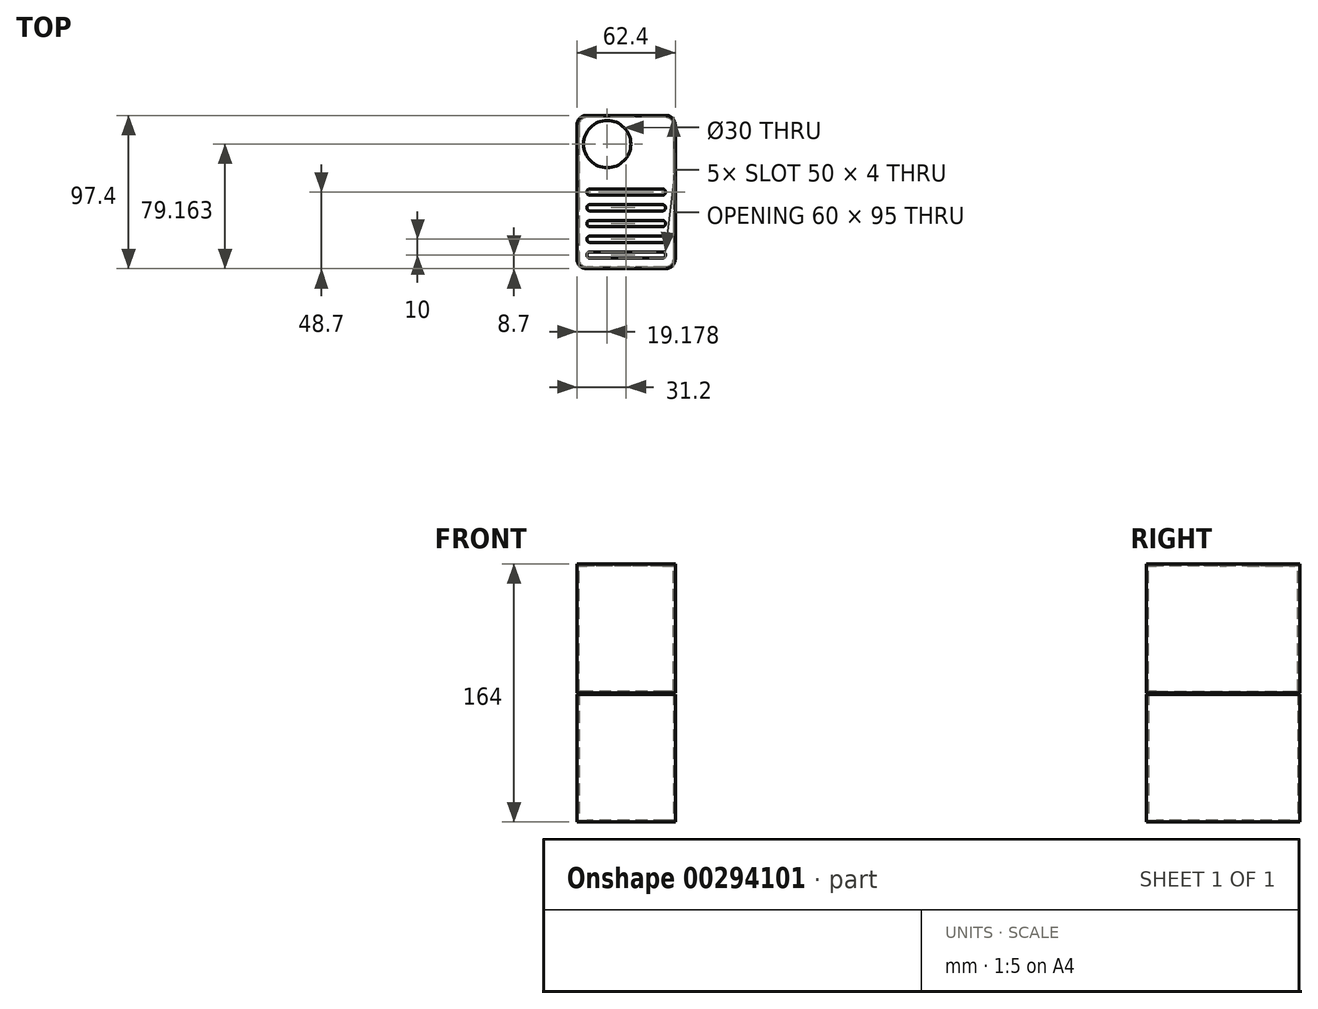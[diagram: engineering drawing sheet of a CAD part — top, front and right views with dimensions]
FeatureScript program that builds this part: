
annotation { "Feature Type Name" : "Feature", "Feature Type Description" : "" }
export const myFeature = defineFeature(function(context is Context, id is Id, definition is map)
    precondition{}
    {
        {
            var Q0;
            Q0=qCreatedBy(makeId("Top.planeOp"),FACE);
            var sketch = newSketch(context, id + "F0", { "sketchPlane" : qUnion([Q0])});
            skLineSegment(sketch, "E0.bottom", {"start": v(25, 47.5) * mm, "end": v(-25, 47.5) * mm});
            skLineSegment(sketch, "E0.top", {"start": v(25, -47.5) * mm, "end": v(-25, -47.5) * mm});
            skLineSegment(sketch, "E0.left", {"start": v(30, 42.5) * mm, "end": v(30, -42.5) * mm});
            skLineSegment(sketch, "E0.right", {"start": v(-30, 42.5) * mm, "end": v(-30, -42.5) * mm});
            skPoint(sketch, "E0.middle", {"position": v(0, 0) * mm});
            skPoint(sketch, "E1.visualSharp", {"position": v(-30, 47.5) * mm});
            skArc(sketch, "E1.filletArc", {"start": v(-25, 47.5) * mm, "mid": v(-28.54, 46.04) * mm, "end": v(-30, 42.5) * mm});
            skPoint(sketch, "E2.visualSharp", {"position": v(30, 47.5) * mm});
            skArc(sketch, "E2.filletArc", {"start": v(30, 42.5) * mm, "mid": v(28.54, 46.04) * mm, "end": v(25, 47.5) * mm});
            skPoint(sketch, "E3.visualSharp", {"position": v(30, -47.5) * mm});
            skArc(sketch, "E3.filletArc", {"start": v(25, -47.5) * mm, "mid": v(28.54, -46.04) * mm, "end": v(30, -42.5) * mm});
            skPoint(sketch, "E4.visualSharp", {"position": v(-30, -47.5) * mm});
            skArc(sketch, "E4.filletArc", {"start": v(-30, -42.5) * mm, "mid": v(-28.54, -46.04) * mm, "end": v(-25, -47.5) * mm});
            skArc(sketch, "E5.0", {"start": v(31.2, 42.5) * mm, "mid": v(29.38, 46.88) * mm, "end": v(25, 48.7) * mm});
            skLineSegment(sketch, "E5.1", {"start": v(31.2, 42.5) * mm, "end": v(31.2, -42.5) * mm});
            skLineSegment(sketch, "E5.2", {"start": v(25, 48.7) * mm, "end": v(-25, 48.7) * mm});
            skArc(sketch, "E5.3", {"start": v(25, -48.7) * mm, "mid": v(29.38, -46.88) * mm, "end": v(31.2, -42.5) * mm});
            skArc(sketch, "E5.4", {"start": v(-25, 48.7) * mm, "mid": v(-29.38, 46.88) * mm, "end": v(-31.2, 42.5) * mm});
            skLineSegment(sketch, "E5.5", {"start": v(-31.2, 42.5) * mm, "end": v(-31.2, -42.5) * mm});
            skArc(sketch, "E5.6", {"start": v(-31.2, -42.5) * mm, "mid": v(-29.38, -46.88) * mm, "end": v(-25, -48.7) * mm});
            skLineSegment(sketch, "E5.7", {"start": v(25, -48.7) * mm, "end": v(-25, -48.7) * mm});
            skSolve(sketch);
        }
        {
            var Q0;
            Q0 = qSketchRegion(id + "F0", true);
            extrude(context, id + "F1", {"entities" : qUnion([Q0]), "depth" : 82 * mm});
        }
        {
            var Q0;
            Q0=makeQuery(id+"F0.imprint","IMPRINT",FACE,{"disambiguationData":[TD([[makeQuery(id+"F0.imprint","IMPRINT",EDGE,{"derivedFrom":sQuery(id+"F0.wireOp",EDGE,"E0.bottom")}),1.0]])]});
            extrude(context, id + "F2", {"entities" : qUnion([Q0]), "operationType" : NewBodyOperationType.ADD, "depth" : 1.2 * mm});
        }
        {
            var Q0;
            Q0=makeQuery(id+"F1.opExtrude","CAP_FACE",FACE,{"disambiguationData":[OSD([sQuery(id+"F0.wireOp",EDGE,"E0.bottom"),sQuery(id+"F0.wireOp",EDGE,"E0.top"),sQuery(id+"F0.wireOp",EDGE,"E0.left"),sQuery(id+"F0.wireOp",EDGE,"E0.right"),sQuery(id+"F0.wireOp",EDGE,"E1.filletArc"),sQuery(id+"F0.wireOp",EDGE,"E2.filletArc"),sQuery(id+"F0.wireOp",EDGE,"E3.filletArc"),sQuery(id+"F0.wireOp",EDGE,"E4.filletArc"),sQuery(id+"F0.wireOp",EDGE,"E5.0"),sQuery(id+"F0.wireOp",EDGE,"E5.1"),sQuery(id+"F0.wireOp",EDGE,"E5.2"),sQuery(id+"F0.wireOp",EDGE,"E5.3"),sQuery(id+"F0.wireOp",EDGE,"E5.4"),sQuery(id+"F0.wireOp",EDGE,"E5.5"),sQuery(id+"F0.wireOp",EDGE,"E5.6"),sQuery(id+"F0.wireOp",EDGE,"E5.7")])],"isStart":false});
            var sketch = newSketch(context, id + "F3", { "sketchPlane" : qUnion([Q0])});
            skArc(sketch, "E6.0", {"start": v(-30.5, -42.5) * mm, "mid": v(-28.89, -46.39) * mm, "end": v(-25, -48) * mm});
            skLineSegment(sketch, "E6.1", {"start": v(-30.5, 42.5) * mm, "end": v(-30.5, -42.5) * mm});
            skLineSegment(sketch, "E6.2", {"start": v(-25, -48) * mm, "end": v(25, -48) * mm});
            skArc(sketch, "E6.3", {"start": v(-25, 48) * mm, "mid": v(-28.89, 46.39) * mm, "end": v(-30.5, 42.5) * mm});
            skArc(sketch, "E6.4", {"start": v(25, -48) * mm, "mid": v(28.89, -46.39) * mm, "end": v(30.5, -42.5) * mm});
            skLineSegment(sketch, "E6.5", {"start": v(30.5, -42.5) * mm, "end": v(30.5, 42.5) * mm});
            skArc(sketch, "E6.6", {"start": v(30.5, 42.5) * mm, "mid": v(28.89, 46.39) * mm, "end": v(25, 48) * mm});
            skLineSegment(sketch, "E6.7", {"start": v(25, 48) * mm, "end": v(-25, 48) * mm});
            skSolve(sketch);
        }
        {
            var Q0;
            Q0=makeQuery(id+"F3.imprint","IMPRINT",FACE,{"disambiguationData":[TD([[makeQuery(id+"F3.imprint","IMPRINT",EDGE,{"derivedFrom":sQuery(id+"F3.wireOp",EDGE,"E6.0")}),-1.0]])]});
            extrude(context, id + "F4", {"entities" : qUnion([Q0]), "operationType" : NewBodyOperationType.REMOVE, "oppositeDirection" : true, "depth" : 1 * mm});
        }
        {
            var Q0;
            Q0=makeQuery(id+"F1.opExtrude","SWEPT_BODY",BODY,{"disambiguationData":[OSD([sQuery(id+"F0.wireOp",EDGE,"E0.bottom"),sQuery(id+"F0.wireOp",EDGE,"E0.top"),sQuery(id+"F0.wireOp",EDGE,"E0.left"),sQuery(id+"F0.wireOp",EDGE,"E0.right"),sQuery(id+"F0.wireOp",EDGE,"E1.filletArc"),sQuery(id+"F0.wireOp",EDGE,"E2.filletArc"),sQuery(id+"F0.wireOp",EDGE,"E3.filletArc"),sQuery(id+"F0.wireOp",EDGE,"E4.filletArc"),sQuery(id+"F0.wireOp",EDGE,"E5.0"),sQuery(id+"F0.wireOp",EDGE,"E5.1"),sQuery(id+"F0.wireOp",EDGE,"E5.2"),sQuery(id+"F0.wireOp",EDGE,"E5.3"),sQuery(id+"F0.wireOp",EDGE,"E5.4"),sQuery(id+"F0.wireOp",EDGE,"E5.5"),sQuery(id+"F0.wireOp",EDGE,"E5.6"),sQuery(id+"F0.wireOp",EDGE,"E5.7")])]});
            var Q1;
            Q1=makeQuery(id+"F1.opExtrude","CAP_FACE",FACE,{"disambiguationData":[OSD([sQuery(id+"F0.wireOp",EDGE,"E0.bottom"),sQuery(id+"F0.wireOp",EDGE,"E0.top"),sQuery(id+"F0.wireOp",EDGE,"E0.left"),sQuery(id+"F0.wireOp",EDGE,"E0.right"),sQuery(id+"F0.wireOp",EDGE,"E1.filletArc"),sQuery(id+"F0.wireOp",EDGE,"E2.filletArc"),sQuery(id+"F0.wireOp",EDGE,"E3.filletArc"),sQuery(id+"F0.wireOp",EDGE,"E4.filletArc"),sQuery(id+"F0.wireOp",EDGE,"E5.0"),sQuery(id+"F0.wireOp",EDGE,"E5.1"),sQuery(id+"F0.wireOp",EDGE,"E5.2"),sQuery(id+"F0.wireOp",EDGE,"E5.3"),sQuery(id+"F0.wireOp",EDGE,"E5.4"),sQuery(id+"F0.wireOp",EDGE,"E5.5"),sQuery(id+"F0.wireOp",EDGE,"E5.6"),sQuery(id+"F0.wireOp",EDGE,"E5.7")])],"isStart":false});
            mirror(context, id + "F5", {"entities" : qUnion([Q0]), "mirrorPlane" : qUnion([Q1])});
        }
        {
            var Q0;
            Q0=makeQuery(id+"F5.opPattern","COPY",FACE,{"derivedFrom":makeQuery(id+"F4.boolean.opBoolean","COPY",FACE,{"derivedFrom":makeQuery(id+"F4.opExtrude","CAP_FACE",FACE,{"disambiguationData":[OSD([sQuery(id+"F0.wireOp",EDGE,"E5.0"),sQuery(id+"F0.wireOp",EDGE,"E5.1"),sQuery(id+"F0.wireOp",EDGE,"E5.2"),sQuery(id+"F0.wireOp",EDGE,"E5.3"),sQuery(id+"F0.wireOp",EDGE,"E5.4"),sQuery(id+"F0.wireOp",EDGE,"E5.5"),sQuery(id+"F0.wireOp",EDGE,"E5.6"),sQuery(id+"F0.wireOp",EDGE,"E5.7"),sQuery(id+"F3.wireOp",EDGE,"E6.0"),sQuery(id+"F3.wireOp",EDGE,"E6.1"),sQuery(id+"F3.wireOp",EDGE,"E6.2"),sQuery(id+"F3.wireOp",EDGE,"E6.3"),sQuery(id+"F3.wireOp",EDGE,"E6.4"),sQuery(id+"F3.wireOp",EDGE,"E6.5"),sQuery(id+"F3.wireOp",EDGE,"E6.6"),sQuery(id+"F3.wireOp",EDGE,"E6.7")])],"isStart":false})}),"instanceName":"1"});
            var sketch = newSketch(context, id + "F6", { "sketchPlane" : qUnion([Q0])});
            skArc(sketch, "E7.0", {"start": v(30.7, 42.5) * mm, "mid": v(29.03, 46.53) * mm, "end": v(25, 48.2) * mm});
            skLineSegment(sketch, "E7.1", {"start": v(30.7, -42.5) * mm, "end": v(30.7, 42.5) * mm});
            skLineSegment(sketch, "E7.2", {"start": v(25, 48.2) * mm, "end": v(-25, 48.2) * mm});
            skArc(sketch, "E7.3", {"start": v(25, -48.2) * mm, "mid": v(29.03, -46.53) * mm, "end": v(30.7, -42.5) * mm});
            skArc(sketch, "E7.4", {"start": v(-25, 48.2) * mm, "mid": v(-29.03, 46.53) * mm, "end": v(-30.7, 42.5) * mm});
            skLineSegment(sketch, "E7.5", {"start": v(-30.7, 42.5) * mm, "end": v(-30.7, -42.5) * mm});
            skArc(sketch, "E7.6", {"start": v(-30.7, -42.5) * mm, "mid": v(-29.03, -46.53) * mm, "end": v(-25, -48.2) * mm});
            skLineSegment(sketch, "E7.7", {"start": v(-25, -48.2) * mm, "end": v(25, -48.2) * mm});
            skSolve(sketch);
        }
        {
            var Q0;
            Q0=makeQuery(id+"F6.imprint","IMPRINT",FACE,{"disambiguationData":[TD([[makeQuery(id+"F6.imprint","IMPRINT",EDGE,{"derivedFrom":sQuery(id+"F6.wireOp",EDGE,"E7.0")}),-1.0]])]});
            extrude(context, id + "F7", {"entities" : qUnion([Q0]), "operationType" : NewBodyOperationType.ADD, "depth" : 1 * mm});
        }
        {
            var Q0;
            Q0=makeQuery(id+"F5.opPattern","COPY",FACE,{"derivedFrom":makeQuery(id+"F1.opExtrude","CAP_FACE",FACE,{"disambiguationData":[OSD([sQuery(id+"F0.wireOp",EDGE,"E0.bottom"),sQuery(id+"F0.wireOp",EDGE,"E0.top"),sQuery(id+"F0.wireOp",EDGE,"E0.left"),sQuery(id+"F0.wireOp",EDGE,"E0.right"),sQuery(id+"F0.wireOp",EDGE,"E1.filletArc"),sQuery(id+"F0.wireOp",EDGE,"E2.filletArc"),sQuery(id+"F0.wireOp",EDGE,"E3.filletArc"),sQuery(id+"F0.wireOp",EDGE,"E4.filletArc"),sQuery(id+"F0.wireOp",EDGE,"E5.0"),sQuery(id+"F0.wireOp",EDGE,"E5.1"),sQuery(id+"F0.wireOp",EDGE,"E5.2"),sQuery(id+"F0.wireOp",EDGE,"E5.3"),sQuery(id+"F0.wireOp",EDGE,"E5.4"),sQuery(id+"F0.wireOp",EDGE,"E5.5"),sQuery(id+"F0.wireOp",EDGE,"E5.6"),sQuery(id+"F0.wireOp",EDGE,"E5.7")])],"isStart":false}),"instanceName":"1"});
            extrude(context, id + "F8", {"entities" : qUnion([Q0]), "operationType" : NewBodyOperationType.REMOVE, "oppositeDirection" : true, "depth" : 1 * mm});
        }
        {
            var Q0;
            {var subQ0=sQuery(id+"F0.wireOp",EDGE,"E4.filletArc");var subQ1=sQuery(id+"F0.wireOp",EDGE,"E3.filletArc");var subQ2=sQuery(id+"F0.wireOp",EDGE,"E2.filletArc");var subQ3=sQuery(id+"F0.wireOp",EDGE,"E1.filletArc");var subQ4=sQuery(id+"F0.wireOp",EDGE,"E0.right");var subQ5=sQuery(id+"F0.wireOp",EDGE,"E0.left");var subQ6=sQuery(id+"F0.wireOp",EDGE,"E0.top");var subQ7=sQuery(id+"F0.wireOp",EDGE,"E0.bottom");Q0=makeQuery(id+"F5.opPattern","COPY",FACE,{"derivedFrom":makeQuery(id+"F2.boolean.opBoolean","MERGE",FACE,{"derivedFrom":[makeQuery(id+"F1.opExtrude","CAP_FACE",FACE,{"disambiguationData":[OSD([subQ7,subQ6,subQ5,subQ4,subQ3,subQ2,subQ1,subQ0,sQuery(id+"F0.wireOp",EDGE,"E5.0"),sQuery(id+"F0.wireOp",EDGE,"E5.1"),sQuery(id+"F0.wireOp",EDGE,"E5.2"),sQuery(id+"F0.wireOp",EDGE,"E5.3"),sQuery(id+"F0.wireOp",EDGE,"E5.4"),sQuery(id+"F0.wireOp",EDGE,"E5.5"),sQuery(id+"F0.wireOp",EDGE,"E5.6"),sQuery(id+"F0.wireOp",EDGE,"E5.7")])],"isStart":true}),makeQuery(id+"F2.opExtrude","CAP_FACE",FACE,{"disambiguationData":[OSD([subQ7,subQ6,subQ5,subQ4,subQ3,subQ2,subQ1,subQ0])],"isStart":true})]}),"instanceName":"1"});}
            var sketch = newSketch(context, id + "F9", { "sketchPlane" : qUnion([Q0])});
            skLineSegment(sketch, "E8.bottom", {"start": v(23, 2) * mm, "end": v(-23, 2) * mm});
            skLineSegment(sketch, "E8.top", {"start": v(23, -2) * mm, "end": v(-23, -2) * mm});
            skLineSegment(sketch, "E8.left", {"start": v(25, 0) * mm, "end": v(25, 0) * mm});
            skLineSegment(sketch, "E8.right", {"start": v(-25, 0) * mm, "end": v(-25, 0) * mm});
            skPoint(sketch, "E8.middle", {"position": v(0, 0) * mm});
            skPoint(sketch, "E9.visualSharp", {"position": v(-25, 2) * mm});
            skArc(sketch, "E9.filletArc", {"start": v(-23, 2) * mm, "mid": v(-24.41, 1.41) * mm, "end": v(-25, 0) * mm});
            skPoint(sketch, "E10.visualSharp", {"position": v(-25, -2) * mm});
            skArc(sketch, "E10.filletArc", {"start": v(-25, 0) * mm, "mid": v(-24.41, -1.41) * mm, "end": v(-23, -2) * mm});
            skPoint(sketch, "E11.visualSharp", {"position": v(25, 2) * mm});
            skArc(sketch, "E11.filletArc", {"start": v(25, 0) * mm, "mid": v(24.41, 1.41) * mm, "end": v(23, 2) * mm});
            skPoint(sketch, "E12.visualSharp", {"position": v(25, -2) * mm});
            skArc(sketch, "E12.filletArc", {"start": v(23, -2) * mm, "mid": v(24.41, -1.41) * mm, "end": v(25, 0) * mm});
            skLineSegment(sketch, "E13.direction1", {"start": v(-25, -2) * mm, "end": v(0, -2) * mm, "construction": true});
            skLineSegment(sketch, "E13.direction2", {"start": v(-25, -2) * mm, "end": v(-25, 8) * mm, "construction": true});
            skArc(sketch, "E14.0.1.0", {"start": v(-25, -10) * mm, "mid": v(-24.41, -11.41) * mm, "end": v(-23, -12) * mm});
            skArc(sketch, "E14.0.1.1", {"start": v(-23, -8) * mm, "mid": v(-24.41, -8.59) * mm, "end": v(-25, -10) * mm});
            skLineSegment(sketch, "E14.0.1.2", {"start": v(23, -8) * mm, "end": v(-23, -8) * mm});
            skArc(sketch, "E14.0.1.3", {"start": v(25, -10) * mm, "mid": v(24.41, -8.59) * mm, "end": v(23, -8) * mm});
            skArc(sketch, "E14.0.1.4", {"start": v(23, -12) * mm, "mid": v(24.41, -11.41) * mm, "end": v(25, -10) * mm});
            skLineSegment(sketch, "E14.0.1.5", {"start": v(23, -12) * mm, "end": v(-23, -12) * mm});
            skArc(sketch, "E14.0.2.0", {"start": v(-25, -20) * mm, "mid": v(-24.41, -21.41) * mm, "end": v(-23, -22) * mm});
            skArc(sketch, "E14.0.2.1", {"start": v(-23, -18) * mm, "mid": v(-24.41, -18.59) * mm, "end": v(-25, -20) * mm});
            skLineSegment(sketch, "E14.0.2.2", {"start": v(23, -18) * mm, "end": v(-23, -18) * mm});
            skArc(sketch, "E14.0.2.3", {"start": v(25, -20) * mm, "mid": v(24.41, -18.59) * mm, "end": v(23, -18) * mm});
            skArc(sketch, "E14.0.2.4", {"start": v(23, -22) * mm, "mid": v(24.41, -21.41) * mm, "end": v(25, -20) * mm});
            skLineSegment(sketch, "E14.0.2.5", {"start": v(23, -22) * mm, "end": v(-23, -22) * mm});
            skArc(sketch, "E14.0.3.0", {"start": v(-25, -30) * mm, "mid": v(-24.41, -31.41) * mm, "end": v(-23, -32) * mm});
            skArc(sketch, "E14.0.3.1", {"start": v(-23, -28) * mm, "mid": v(-24.41, -28.59) * mm, "end": v(-25, -30) * mm});
            skLineSegment(sketch, "E14.0.3.2", {"start": v(23, -28) * mm, "end": v(-23, -28) * mm});
            skArc(sketch, "E14.0.3.3", {"start": v(25, -30) * mm, "mid": v(24.41, -28.59) * mm, "end": v(23, -28) * mm});
            skArc(sketch, "E14.0.3.4", {"start": v(23, -32) * mm, "mid": v(24.41, -31.41) * mm, "end": v(25, -30) * mm});
            skLineSegment(sketch, "E14.0.3.5", {"start": v(23, -32) * mm, "end": v(-23, -32) * mm});
            skArc(sketch, "E14.0.4.0", {"start": v(-25, -40) * mm, "mid": v(-24.41, -41.41) * mm, "end": v(-23, -42) * mm});
            skArc(sketch, "E14.0.4.1", {"start": v(-23, -38) * mm, "mid": v(-24.41, -38.59) * mm, "end": v(-25, -40) * mm});
            skLineSegment(sketch, "E14.0.4.2", {"start": v(23, -38) * mm, "end": v(-23, -38) * mm});
            skArc(sketch, "E14.0.4.3", {"start": v(25, -40) * mm, "mid": v(24.41, -38.59) * mm, "end": v(23, -38) * mm});
            skArc(sketch, "E14.0.4.4", {"start": v(23, -42) * mm, "mid": v(24.41, -41.41) * mm, "end": v(25, -40) * mm});
            skLineSegment(sketch, "E14.0.4.5", {"start": v(23, -42) * mm, "end": v(-23, -42) * mm});
            skLineSegment(sketch, "E14.direction1", {"start": v(-23, -2) * mm, "end": v(2, -2) * mm, "construction": true});
            skLineSegment(sketch, "E14.direction2", {"start": v(-23, -2) * mm, "end": v(-23, -12) * mm, "construction": true});
            skCircle(sketch, "E15", {"center": v(-12.02, 30.46) * mm, "radius": 15 * mm});
            skLineSegment(sketch, "E16.0.0.1", {"start": v(23, 12) * mm, "end": v(-23, 12) * mm});
            skPoint(sketch, "E16.3.0.1", {"position": v(0, 10) * mm});
            skPoint(sketch, "E16.4.0.1", {"position": v(25, 12) * mm});
            skPoint(sketch, "E16.5.0.1", {"position": v(-25, 8) * mm});
            skPoint(sketch, "E16.6.0.1", {"position": v(-25, 12) * mm});
            skLineSegment(sketch, "E16.7.0.1", {"start": v(23, 8) * mm, "end": v(-23, 8) * mm});
            skPoint(sketch, "E16.10.0.1", {"position": v(25, 8) * mm});
            skArc(sketch, "E16.11.0.1", {"start": v(-25, 10) * mm, "mid": v(-24.41, 8.59) * mm, "end": v(-23, 8) * mm});
            skArc(sketch, "E16.15.0.1", {"start": v(25, 10) * mm, "mid": v(24.41, 11.41) * mm, "end": v(23, 12) * mm});
            skArc(sketch, "E16.19.0.1", {"start": v(23, 8) * mm, "mid": v(24.41, 8.59) * mm, "end": v(25, 10) * mm});
            skArc(sketch, "E16.23.0.1", {"start": v(-23, 12) * mm, "mid": v(-24.41, 11.41) * mm, "end": v(-25, 10) * mm});
            skSolve(sketch);
        }
        {
            var Q0;
            Q0=makeQuery(id+"F9.imprint","IMPRINT",FACE,{"disambiguationData":[TD([[makeQuery(id+"F9.imprint","IMPRINT",EDGE,{"derivedFrom":sQuery(id+"F9.wireOp",EDGE,"E15")}),1.0]])]});
            var Q1;
            Q1=makeQuery(id+"F9.imprint","IMPRINT",FACE,{"disambiguationData":[TD([[makeQuery(id+"F9.imprint","IMPRINT",EDGE,{"derivedFrom":sQuery(id+"F9.wireOp",EDGE,"E13.0.2.0")}),1.0]])]});
            var Q2;
            Q2=makeQuery(id+"F9.imprint","IMPRINT",FACE,{"disambiguationData":[TD([[makeQuery(id+"F9.imprint","IMPRINT",EDGE,{"derivedFrom":sQuery(id+"F9.wireOp",EDGE,"E13.0.1.0")}),1.0]])]});
            var Q3;
            Q3=makeQuery(id+"F9.imprint","IMPRINT",FACE,{"disambiguationData":[TD([[makeQuery(id+"F9.imprint","IMPRINT",EDGE,{"derivedFrom":sQuery(id+"F9.wireOp",EDGE,"E8.bottom")}),1.0]])]});
            var Q4;
            Q4=makeQuery(id+"F9.imprint","IMPRINT",FACE,{"disambiguationData":[TD([[makeQuery(id+"F9.imprint","IMPRINT",EDGE,{"derivedFrom":sQuery(id+"F9.wireOp",EDGE,"E14.0.1.0")}),1.0]])]});
            var Q5;
            Q5=makeQuery(id+"F9.imprint","IMPRINT",FACE,{"disambiguationData":[TD([[makeQuery(id+"F9.imprint","IMPRINT",EDGE,{"derivedFrom":sQuery(id+"F9.wireOp",EDGE,"E14.0.2.0")}),1.0]])]});
            var Q6;
            Q6=makeQuery(id+"F9.imprint","IMPRINT",FACE,{"disambiguationData":[TD([[makeQuery(id+"F9.imprint","IMPRINT",EDGE,{"derivedFrom":sQuery(id+"F9.wireOp",EDGE,"E14.0.3.0")}),1.0]])]});
            var Q7;
            Q7=makeQuery(id+"F9.imprint","IMPRINT",FACE,{"disambiguationData":[TD([[makeQuery(id+"F9.imprint","IMPRINT",EDGE,{"derivedFrom":sQuery(id+"F9.wireOp",EDGE,"E14.0.4.0")}),1.0]])]});
            extrude(context, id + "F10", {"entities" : qUnion([Q0, Q1, Q2, Q3, Q4, Q5, Q6, Q7]), "operationType" : NewBodyOperationType.REMOVE, "oppositeDirection" : true, "depth" : 1.2 * mm});
        }
    });
